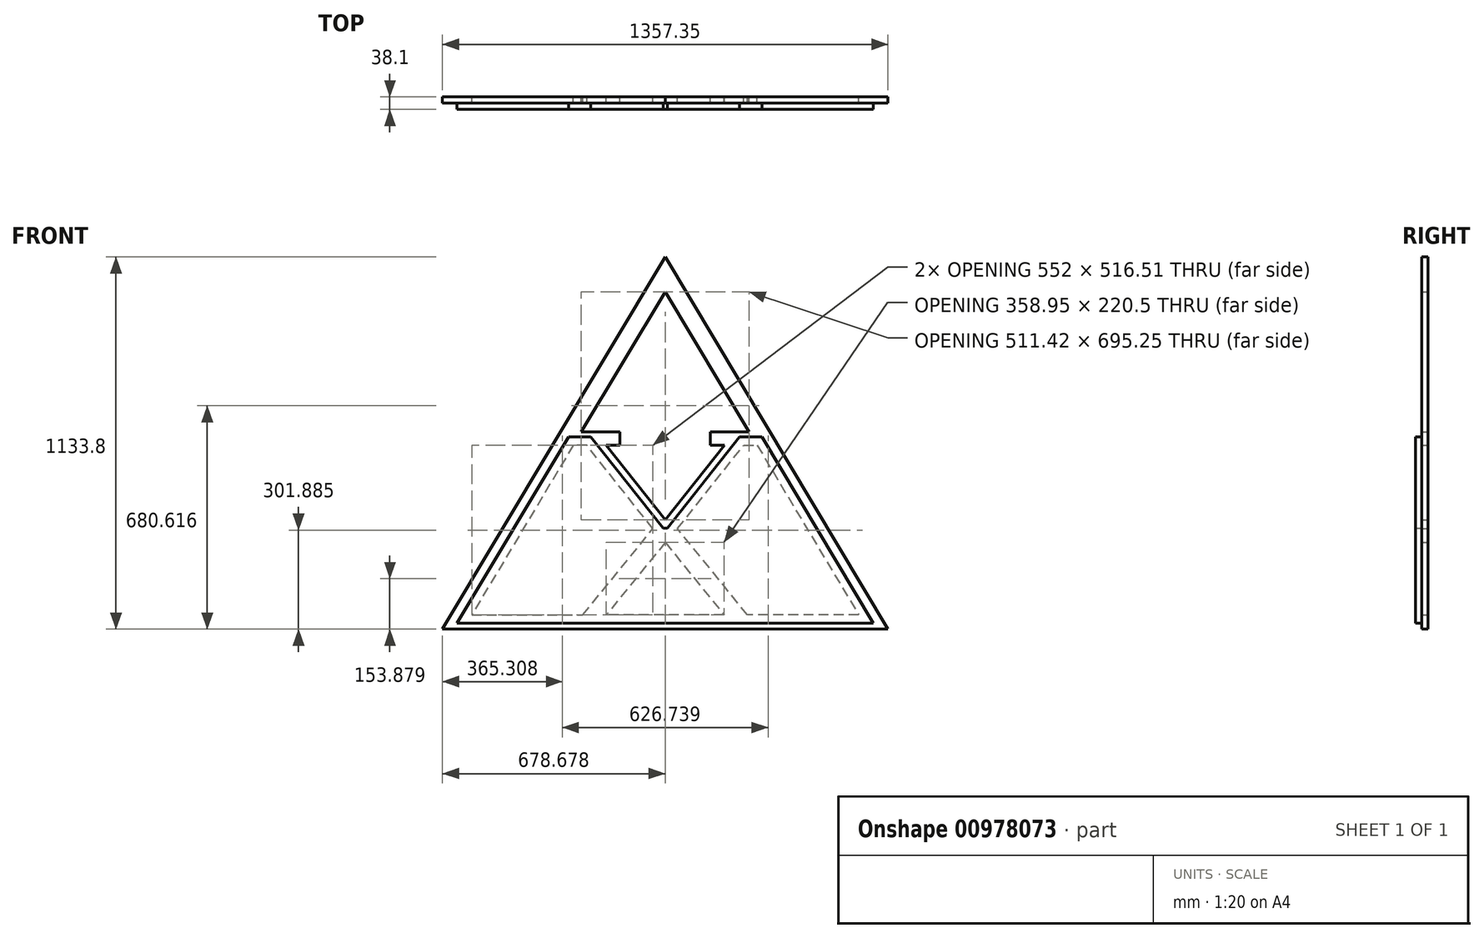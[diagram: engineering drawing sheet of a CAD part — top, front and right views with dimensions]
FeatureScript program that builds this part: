
annotation { "Feature Type Name" : "Feature", "Feature Type Description" : "" }
export const myFeature = defineFeature(function(context is Context, id is Id, definition is map)
    precondition{}
    {
        {
            var Q0;
            Q0=qCreatedBy(makeId("Front.planeOp"),FACE);
            var sketch = newSketch(context, id + "F0", { "sketchPlane" : qUnion([Q0])});
            skLineSegment(sketch, "E0", {"start": v(695.5, -24.8) * mm, "end": v(16.83, -1158.61) * mm});
            skLineSegment(sketch, "E1", {"start": v(695.5, -24.8) * mm, "end": v(695.5, -1264.7) * mm, "construction": true});
            skLineSegment(sketch, "E2", {"start": v(16.83, -1158.61) * mm, "end": v(695.5, -1158.61) * mm});
            skLineSegment(sketch, "E3", {"start": v(695.5, -894.48) * mm, "end": v(516.03, -1114.98) * mm});
            skLineSegment(sketch, "E4", {"start": v(516.03, -1114.98) * mm, "end": v(695.5, -1114.98) * mm});
            skLineSegment(sketch, "E5", {"start": v(658.14, -852.84) * mm, "end": v(456.41, -598.47) * mm});
            skLineSegment(sketch, "E6", {"start": v(456.41, -598.47) * mm, "end": v(415.31, -598.47) * mm});
            skLineSegment(sketch, "E7", {"start": v(415.31, -598.47) * mm, "end": v(106.14, -1114.98) * mm});
            skLineSegment(sketch, "E8", {"start": v(106.14, -1114.98) * mm, "end": v(444.77, -1114.98) * mm});
            skLineSegment(sketch, "E9", {"start": v(444.77, -1114.98) * mm, "end": v(658.14, -852.84) * mm});
            skLineSegment(sketch, "E10", {"start": v(695.5, -825.62) * mm, "end": v(515.37, -598.47) * mm});
            skLineSegment(sketch, "E11", {"start": v(515.37, -598.47) * mm, "end": v(557.8, -598.47) * mm});
            skLineSegment(sketch, "E12", {"start": v(557.8, -598.47) * mm, "end": v(557.8, -557.56) * mm});
            skLineSegment(sketch, "E13", {"start": v(557.8, -557.56) * mm, "end": v(439.8, -557.56) * mm});
            skLineSegment(sketch, "E14", {"start": v(439.8, -557.56) * mm, "end": v(695.5, -130.37) * mm});
            skLineSegment(sketch, "E15.MirrorCS", {"start": v(951.22, -557.56) * mm, "end": v(695.5, -130.37) * mm});
            skLineSegment(sketch, "E16.MirrorCS", {"start": v(695.5, -24.8) * mm, "end": v(1374.18, -1158.61) * mm});
            skLineSegment(sketch, "E17.MirrorCS", {"start": v(833.2, -557.56) * mm, "end": v(951.22, -557.56) * mm});
            skLineSegment(sketch, "E18.MirrorCS", {"start": v(833.2, -598.47) * mm, "end": v(833.2, -557.56) * mm});
            skLineSegment(sketch, "E19.MirrorCS", {"start": v(875.65, -598.47) * mm, "end": v(833.2, -598.47) * mm});
            skLineSegment(sketch, "E20.MirrorCS", {"start": v(695.5, -825.62) * mm, "end": v(875.65, -598.47) * mm});
            skLineSegment(sketch, "E21.MirrorCS", {"start": v(732.88, -852.84) * mm, "end": v(934.6, -598.47) * mm});
            skLineSegment(sketch, "E22.MirrorCS", {"start": v(934.6, -598.47) * mm, "end": v(975.7, -598.47) * mm});
            skLineSegment(sketch, "E23.MirrorCS", {"start": v(975.7, -598.47) * mm, "end": v(1284.88, -1114.98) * mm});
            skLineSegment(sketch, "E24.MirrorCS", {"start": v(1284.88, -1114.98) * mm, "end": v(946.25, -1114.98) * mm});
            skLineSegment(sketch, "E25.MirrorCS", {"start": v(946.25, -1114.98) * mm, "end": v(732.88, -852.84) * mm});
            skLineSegment(sketch, "E26.MirrorCS", {"start": v(695.5, -894.48) * mm, "end": v(874.98, -1114.98) * mm});
            skLineSegment(sketch, "E27.MirrorCS", {"start": v(874.98, -1114.98) * mm, "end": v(695.5, -1114.98) * mm});
            skLineSegment(sketch, "E28.MirrorCS", {"start": v(1374.18, -1158.61) * mm, "end": v(695.5, -1158.61) * mm});
            skSolve(sketch);
        }
        {
            var Q0;
            Q0=makeQuery(id+"F0.imprint","IMPRINT",FACE,{"disambiguationData":[TD([[makeQuery(id+"F0.imprint","IMPRINT",EDGE,{"derivedFrom":sQuery(id+"F0.wireOp",EDGE,"E0")}),1.0]])]});
            extrude(context, id + "F1", {"entities" : qUnion([Q0]), "depth" : 19.05 * mm, "offsetDistance" : 25.4 * mm});
        }
        {
            var Q0;
            Q0=makeQuery(id+"F1.opExtrude","CAP_FACE",FACE,{"disambiguationData":[OSD([sQuery(id+"F0.wireOp",EDGE,"E0"),sQuery(id+"F0.wireOp",EDGE,"E2"),sQuery(id+"F0.wireOp",EDGE,"E3"),sQuery(id+"F0.wireOp",EDGE,"E4"),sQuery(id+"F0.wireOp",EDGE,"E5"),sQuery(id+"F0.wireOp",EDGE,"E6"),sQuery(id+"F0.wireOp",EDGE,"E7"),sQuery(id+"F0.wireOp",EDGE,"E8"),sQuery(id+"F0.wireOp",EDGE,"E9"),sQuery(id+"F0.wireOp",EDGE,"E10"),sQuery(id+"F0.wireOp",EDGE,"E11"),sQuery(id+"F0.wireOp",EDGE,"E12"),sQuery(id+"F0.wireOp",EDGE,"E13"),sQuery(id+"F0.wireOp",EDGE,"E14"),sQuery(id+"F0.wireOp",EDGE,"E15.MirrorCS"),sQuery(id+"F0.wireOp",EDGE,"E16.MirrorCS"),sQuery(id+"F0.wireOp",EDGE,"E17.MirrorCS"),sQuery(id+"F0.wireOp",EDGE,"E18.MirrorCS"),sQuery(id+"F0.wireOp",EDGE,"E19.MirrorCS"),sQuery(id+"F0.wireOp",EDGE,"E20.MirrorCS"),sQuery(id+"F0.wireOp",EDGE,"E21.MirrorCS"),sQuery(id+"F0.wireOp",EDGE,"E22.MirrorCS"),sQuery(id+"F0.wireOp",EDGE,"E23.MirrorCS"),sQuery(id+"F0.wireOp",EDGE,"E24.MirrorCS"),sQuery(id+"F0.wireOp",EDGE,"E25.MirrorCS"),sQuery(id+"F0.wireOp",EDGE,"E26.MirrorCS"),sQuery(id+"F0.wireOp",EDGE,"E27.MirrorCS"),sQuery(id+"F0.wireOp",EDGE,"E28.MirrorCS")])],"isStart":false});
            var sketch = newSketch(context, id + "F2", { "sketchPlane" : qUnion([Q0])});
            skLineSegment(sketch, "E29.0", {"start": v(468.69, -573.07) * mm, "end": v(400.91, -573.07) * mm});
            skLineSegment(sketch, "E29.1", {"start": v(689.12, -851.02) * mm, "end": v(468.69, -573.07) * mm});
            skLineSegment(sketch, "E30", {"start": v(400.91, -573.07) * mm, "end": v(61.33, -1140.38) * mm});
            skLineSegment(sketch, "E31", {"start": v(61.33, -1140.38) * mm, "end": v(1329.69, -1140.38) * mm});
            skLineSegment(sketch, "E32", {"start": v(1329.69, -1140.38) * mm, "end": v(990.1, -573.07) * mm});
            skLineSegment(sketch, "E33", {"start": v(990.1, -573.07) * mm, "end": v(922.33, -573.07) * mm});
            skLineSegment(sketch, "E34", {"start": v(922.33, -573.07) * mm, "end": v(701.9, -851.02) * mm});
            skLineSegment(sketch, "E35", {"start": v(701.9, -851.02) * mm, "end": v(689.12, -851.02) * mm});
            skSolve(sketch);
        }
        {
            var Q0;
            Q0 = qSketchRegion(id + "F2", true);
            extrude(context, id + "F3", {"entities" : qUnion([Q0]), "depth" : 19.05 * mm, "offsetDistance" : 25.4 * mm});
        }
    });
